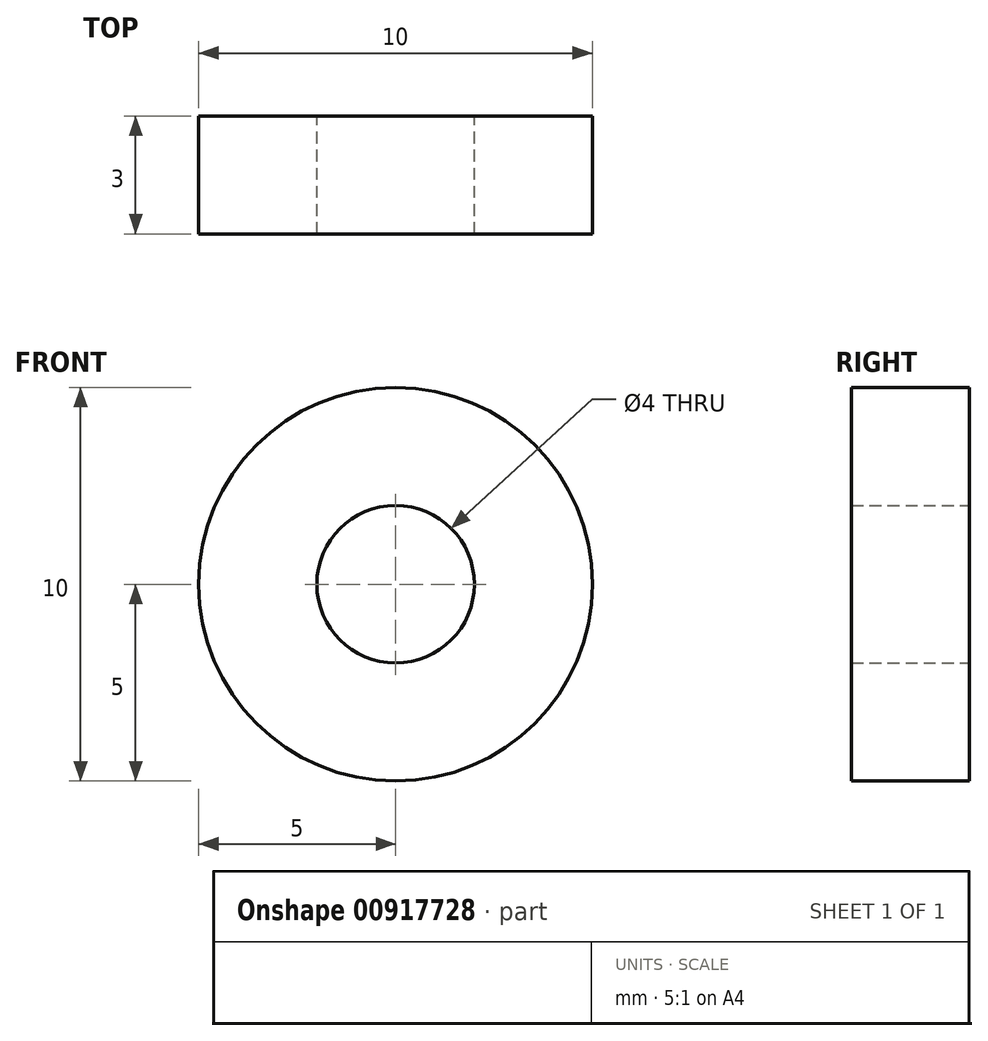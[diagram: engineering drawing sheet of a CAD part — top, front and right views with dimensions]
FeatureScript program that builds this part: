
annotation { "Feature Type Name" : "Feature", "Feature Type Description" : "" }
export const myFeature = defineFeature(function(context is Context, id is Id, definition is map)
    precondition{}
    {
        {
            var Q0;
            Q0=qCreatedBy(makeId("Front.planeOp"),FACE);
            var sketch = newSketch(context, id + "F0", { "sketchPlane" : qUnion([Q0])});
            skCircle(sketch, "E0", {"center": v(0, 0) * mm, "radius": 5 * mm});
            skCircle(sketch, "E1", {"center": v(0, 0) * mm, "radius": 2 * mm});
            skSolve(sketch);
        }
        {
            var Q0;
            Q0=makeQuery(id+"F0.imprint","IMPRINT",FACE,{"disambiguationData":[TD([[makeQuery(id+"F0.imprint","IMPRINT",EDGE,{"derivedFrom":sQuery(id+"F0.wireOp",EDGE,"E0")}),1.0]])]});
            extrude(context, id + "F1", {"entities" : qUnion([Q0]), "depth" : 3 * mm, "offsetDistance" : 25 * mm});
        }
    });
